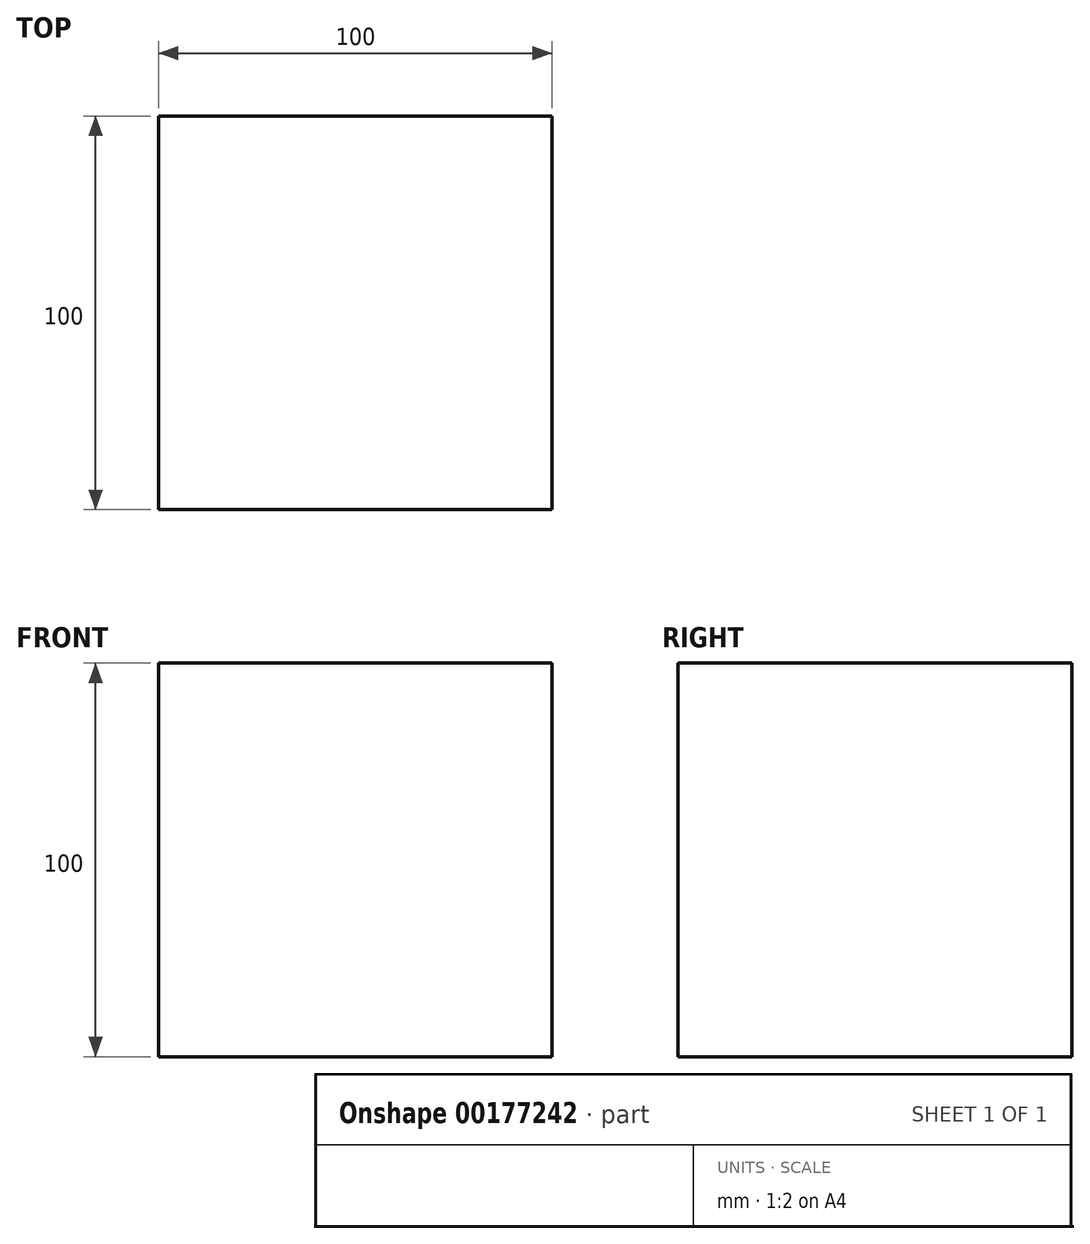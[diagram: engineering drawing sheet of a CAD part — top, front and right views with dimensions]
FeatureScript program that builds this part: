
annotation { "Feature Type Name" : "Feature", "Feature Type Description" : "" }
export const myFeature = defineFeature(function(context is Context, id is Id, definition is map)
    precondition{}
    {
        {
            var Q0;
            Q0=qCreatedBy(makeId("Front.planeOp"),FACE);
            var sketch = newSketch(context, id + "F0", { "sketchPlane" : qUnion([Q0])});
            skLineSegment(sketch, "E0.bottom", {"start": v(-46.36, 46.6) * mm, "end": v(53.64, 46.6) * mm});
            skLineSegment(sketch, "E0.top", {"start": v(-46.36, -53.4) * mm, "end": v(53.64, -53.4) * mm});
            skLineSegment(sketch, "E0.left", {"start": v(-46.36, 46.6) * mm, "end": v(-46.36, -53.4) * mm});
            skLineSegment(sketch, "E0.right", {"start": v(53.64, 46.6) * mm, "end": v(53.64, -53.4) * mm});
            skSolve(sketch);
        }
        {
            var Q0;
            Q0=makeQuery(id+"F0.imprint","IMPRINT",FACE,{"disambiguationData":[TD([[makeQuery(id+"F0.imprint","IMPRINT",EDGE,{"derivedFrom":sQuery(id+"F0.wireOp",EDGE,"E0.bottom")}),-1.0]])]});
            extrude(context, id + "F1", {"entities" : qUnion([Q0]), "depth" : 100 * mm});
        }
    });
